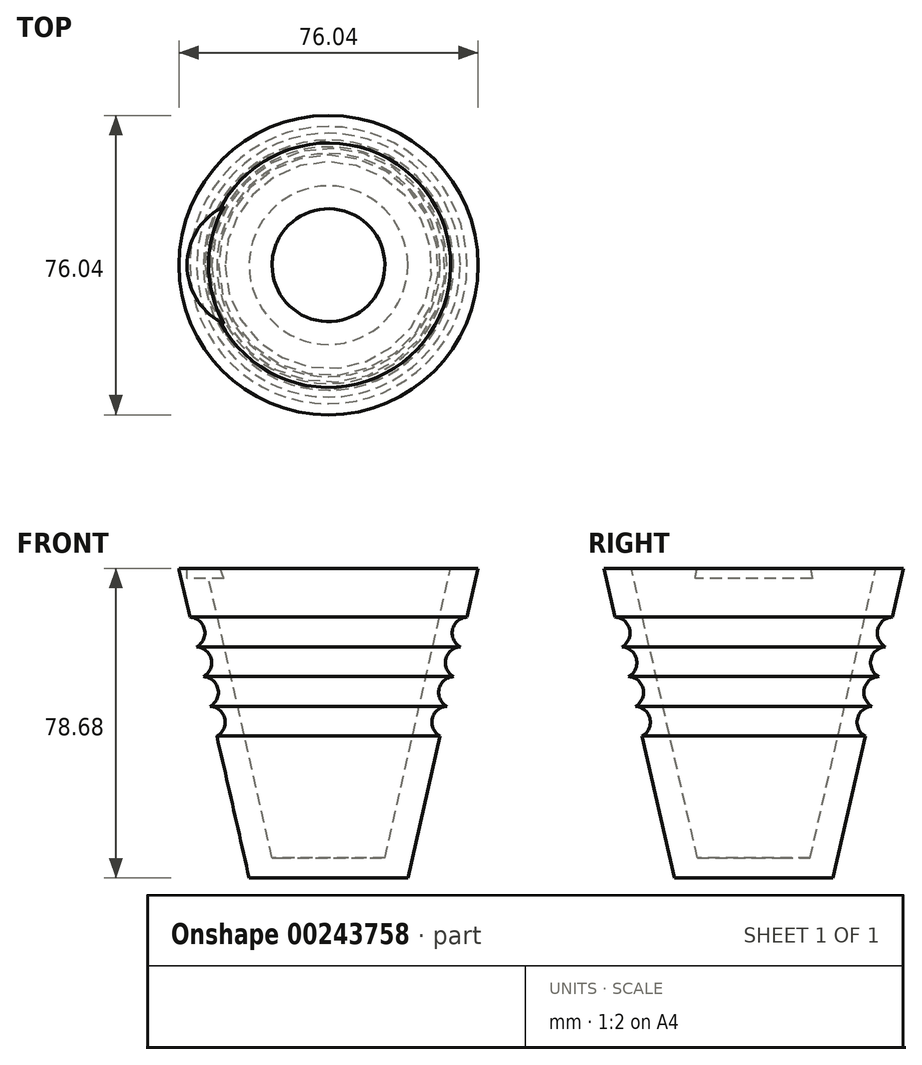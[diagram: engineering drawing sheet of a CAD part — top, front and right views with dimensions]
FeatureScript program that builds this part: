
annotation { "Feature Type Name" : "Feature", "Feature Type Description" : "" }
export const myFeature = defineFeature(function(context is Context, id is Id, definition is map)
    precondition{}
    {
        {
            var Q0;
            Q0=qCreatedBy(makeId("Front.planeOp"),FACE);
            var sketch = newSketch(context, id + "F0", { "sketchPlane" : qUnion([Q0])});
            skLineSegment(sketch, "E0", {"start": v(0, 0) * mm, "end": v(0, 54.9) * mm});
            skLineSegment(sketch, "E1", {"start": v(0, 0) * mm, "end": v(0, -18.58) * mm});
            skLineSegment(sketch, "E2", {"start": v(0, -18.58) * mm, "end": v(14.33, -18.58) * mm});
            skLineSegment(sketch, "E3", {"start": v(18.55, 0) * mm, "end": v(14.33, -18.58) * mm});
            skLineSegment(sketch, "E4", {"start": v(18.55, 0) * mm, "end": v(21.36, 12.38) * mm});
            skLineSegment(sketch, "E5", {"start": v(21.36, 12.38) * mm, "end": v(31.04, 54.99) * mm});
            skLineSegment(sketch, "E6", {"start": v(14.33, -18.58) * mm, "end": v(18.32, -18.58) * mm});
            skLineSegment(sketch, "E7", {"start": v(31.04, 54.99) * mm, "end": v(35.04, 54.99) * mm});
            skLineSegment(sketch, "E8", {"start": v(0, -23.69) * mm, "end": v(0, -18.58) * mm});
            skLineSegment(sketch, "E9", {"start": v(18.32, -18.58) * mm, "end": v(21.31, -18.58) * mm});
            skLineSegment(sketch, "E10", {"start": v(21.31, -18.58) * mm, "end": v(28.34, 12.37) * mm});
            skLineSegment(sketch, "E11", {"start": v(21.31, -18.58) * mm, "end": v(20.15, -23.69) * mm});
            skLineSegment(sketch, "E12", {"start": v(0, -23.69) * mm, "end": v(20.15, -23.69) * mm});
            skLineSegment(sketch, "E13", {"start": v(35.04, 54.99) * mm, "end": v(38.02, 54.99) * mm});
            skArc(sketch, "E14", {"start": v(30.06, 19.93) * mm, "mid": v(26.36, 16.8) * mm, "end": v(28.34, 12.37) * mm});
            skArc(sketch, "E15", {"start": v(31.78, 27.49) * mm, "mid": v(28.08, 24.35) * mm, "end": v(30.06, 19.93) * mm});
            skArc(sketch, "E16", {"start": v(33.5, 35.05) * mm, "mid": v(29.8, 31.91) * mm, "end": v(31.78, 27.49) * mm});
            skArc(sketch, "E17", {"start": v(35.21, 42.6) * mm, "mid": v(31.51, 39.47) * mm, "end": v(33.5, 35.05) * mm});
            skLineSegment(sketch, "E18", {"start": v(35.21, 42.6) * mm, "end": v(38.02, 54.99) * mm});
            skSolve(sketch);
        }
        {
            var Q0;
            {var subQ2=sQuery(id+"F0.wireOp",EDGE,"E6");Q0=makeQuery(id+"F0.imprint","IMPRINT",FACE,{"disambiguationData":[TD([[makeQuery(id+"F0.imprint","IMPRINT",EDGE,{"derivedFrom":subQ2}),-1.0]])]});}
            var Q1;
            Q1=makeQuery(id+"F0.imprint","IMPRINT",FACE,{"disambiguationData":[TD([[makeQuery(id+"F0.imprint","IMPRINT",EDGE,{"derivedFrom":sQuery(id+"F0.wireOp",EDGE,"E3")}),1.0]])]});
            var Q2;
            Q2=sQuery(id+"F0.wireOp",EDGE,"E0");
            revolve(context, id + "F1", {"entities" : qUnion([Q0, Q1]), "axis" : qUnion([Q2]), "revolveType" : RevolveType.FULL});
        }
        {
            var Q0;
            Q0=makeQuery(id+"F1.opRevolve","SWEPT_FACE",FACE,{"disambiguationData":[OSD([sQuery(id+"F0.wireOp",EDGE,"E7"),sQuery(id+"F0.wireOp",EDGE,"E13")])]});
            var sketch = newSketch(context, id + "F2", { "sketchPlane" : qUnion([Q0])});
            skCircle(sketch, "E19", {"center": v(-19.4, 0) * mm, "radius": 16.51 * mm});
            skSolve(sketch);
        }
        {
            var Q0;
            {var subQ0=sQuery(id+"F2.wireOp",EDGE,"E19");var subQ1=makeQuery(id+"F1.opRevolve","SWEPT_EDGE",EDGE,{"disambiguationData":[OSD([sQuery(id+"F0.wireOp",EDGE,"E5"),sQuery(id+"F0.wireOp",EDGE,"E7")])]});var subQ2=makeQuery(id+"F2.imprint","INTERSECT",VERTEX,{"disambiguationData":[OD(0.0)],"derivedFrom":[subQ1,subQ0]});Q0=makeQuery(id+"F2.imprint","IMPRINT",FACE,{"disambiguationData":[TD([[makeQuery(id+"F2.imprint","IMPRINT",EDGE,{"disambiguationData":[TD([[subQ2,-1.0]])],"derivedFrom":subQ0}),1.0]])]});}
            var Q1;
            {var subQ0=sQuery(id+"F2.wireOp",EDGE,"E19");var subQ1=makeQuery(id+"F1.opRevolve","SWEPT_EDGE",EDGE,{"disambiguationData":[OSD([sQuery(id+"F0.wireOp",EDGE,"E5"),sQuery(id+"F0.wireOp",EDGE,"E7")])]});var subQ2=makeQuery(id+"F2.imprint","INTERSECT",VERTEX,{"disambiguationData":[OD(0.0)],"derivedFrom":[subQ1,subQ0]});Q1=makeQuery(id+"F2.imprint","IMPRINT",FACE,{"disambiguationData":[TD([[makeQuery(id+"F2.imprint","IMPRINT",EDGE,{"disambiguationData":[TD([[subQ2,1.0]])],"derivedFrom":subQ0}),1.0]])]});}
            extrude(context, id + "F3", {"entities" : qUnion([Q0, Q1]), "operationType" : NewBodyOperationType.REMOVE, "oppositeDirection" : true, "depth" : 2.54 * mm});
        }
    });
